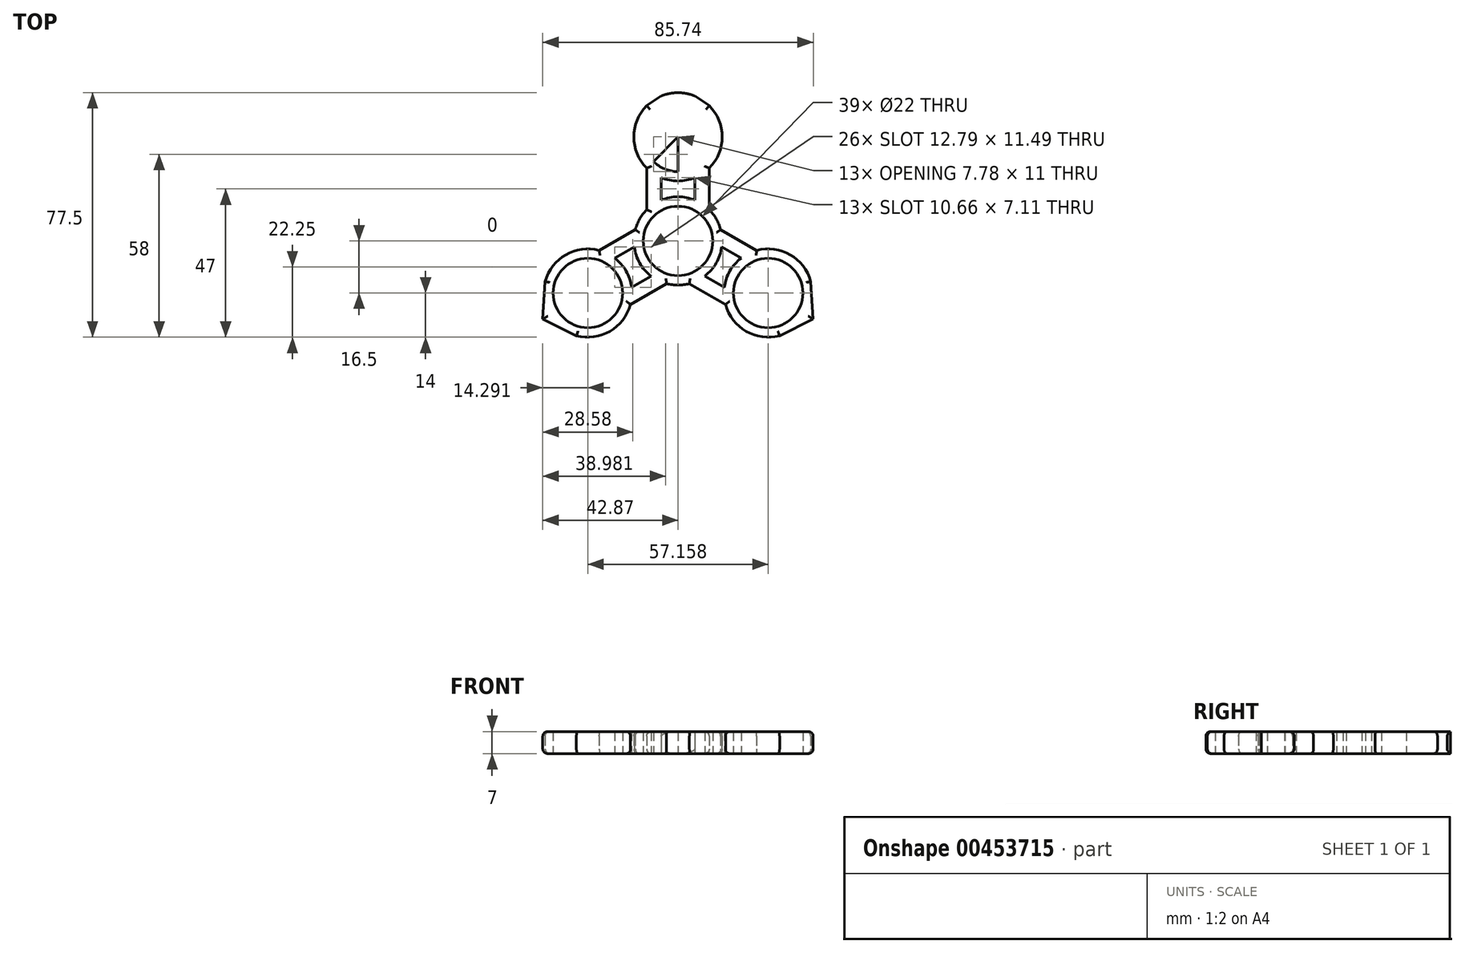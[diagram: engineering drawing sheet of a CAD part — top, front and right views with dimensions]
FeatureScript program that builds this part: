
annotation { "Feature Type Name" : "Feature", "Feature Type Description" : "" }
export const myFeature = defineFeature(function(context is Context, id is Id, definition is map)
    precondition{}
    {
        {
            var Q0;
            Q0=qCreatedBy(makeId("Top.planeOp"),FACE);
            var sketch = newSketch(context, id + "F0", { "sketchPlane" : qUnion([Q0])});
            skCircle(sketch, "E0", {"center": v(0, 0) * mm, "radius": 11 * mm});
            skArc(sketch, "E1.0", {"start": v(-9.9, 9.9) * mm, "mid": v(0, -14) * mm, "end": v(9.9, 9.9) * mm});
            skLineSegment(sketch, "E2", {"start": v(0, 0) * mm, "end": v(9.9, 9.9) * mm});
            skLineSegment(sketch, "E3.MirrorCS", {"start": v(0, 0) * mm, "end": v(-9.9, 9.9) * mm});
            skLineSegment(sketch, "E4", {"start": v(0, 0) * mm, "end": v(0, 16.5) * mm});
            skLineSegment(sketch, "E5", {"start": v(-9.9, 9.9) * mm, "end": v(0, 16.5) * mm});
            skLineSegment(sketch, "E6", {"start": v(0, 16.5) * mm, "end": v(9.9, 9.9) * mm});
            skLineSegment(sketch, "E7", {"start": v(0, 16.5) * mm, "end": v(16.35, 16.5) * mm});
            skLineSegment(sketch, "E8.MirrorCS", {"start": v(0, 33) * mm, "end": v(9.9, 23.1) * mm});
            skCircle(sketch, "E9.MirrorC", {"center": v(0, 33) * mm, "radius": 11 * mm});
            skArc(sketch, "E10.MirrorC", {"start": v(5.33, 20.06) * mm, "mid": v(0, 19) * mm, "end": v(-5.33, 20.06) * mm});
            skLineSegment(sketch, "E11.MirrorCS", {"start": v(0, 33) * mm, "end": v(0, 16.5) * mm});
            skLineSegment(sketch, "E12.MirrorCS", {"start": v(0, 33) * mm, "end": v(-9.9, 23.1) * mm});
            skLineSegment(sketch, "E13.MirrorCS", {"start": v(-9.9, 23.1) * mm, "end": v(0, 16.5) * mm});
            skLineSegment(sketch, "E14.MirrorCS", {"start": v(0, 16.5) * mm, "end": v(9.9, 23.1) * mm});
            skArc(sketch, "E15.trimOffspring", {"start": v(5.33, 12.94) * mm, "mid": v(0, 14) * mm, "end": v(-5.33, 12.94) * mm});
            skArc(sketch, "E16.trimOffspring", {"start": v(-9.9, 23.1) * mm, "mid": v(-14, 33) * mm, "end": v(-9.9, 42.9) * mm});
            skLineSegment(sketch, "E17", {"start": v(5.33, 20.06) * mm, "end": v(5.33, 12.94) * mm});
            skLineSegment(sketch, "E18", {"start": v(9.9, 23.1) * mm, "end": v(9.9, 9.9) * mm});
            skLineSegment(sketch, "E19", {"start": v(-9.9, 23.1) * mm, "end": v(-9.9, 9.9) * mm});
            skLineSegment(sketch, "E20", {"start": v(-5.33, 12.94) * mm, "end": v(-5.33, 20.06) * mm});
            skLineSegment(sketch, "E21", {"start": v(0, 33) * mm, "end": v(7.48, 33) * mm});
            skLineSegment(sketch, "E22.MirrorCS", {"start": v(0, 49.5) * mm, "end": v(9.9, 42.9) * mm});
            skLineSegment(sketch, "E23.MirrorCS", {"start": v(-9.9, 42.9) * mm, "end": v(0, 49.5) * mm});
            skArc(sketch, "E24.trimOffspring", {"start": v(-5.33, 45.94) * mm, "mid": v(0, 47) * mm, "end": v(5.33, 45.94) * mm});
            skArc(sketch, "E25.trimOffspring", {"start": v(9.9, 42.9) * mm, "mid": v(14, 33) * mm, "end": v(9.9, 23.1) * mm});
            skLineSegment(sketch, "E26.1.0", {"start": v(-32.2, -30.02) * mm, "end": v(-42.87, -24.75) * mm});
            skLineSegment(sketch, "E26.1.1", {"start": v(-42.87, -24.75) * mm, "end": v(-42.1, -12.88) * mm});
            skArc(sketch, "E26.1.2", {"start": v(-37.12, -27.6) * mm, "mid": v(-40.7, -23.5) * mm, "end": v(-42.46, -18.35) * mm});
            skArc(sketch, "E26.1.3", {"start": v(-42.1, -12.88) * mm, "mid": v(-35.58, -4.38) * mm, "end": v(-24.96, -2.98) * mm});
            skCircle(sketch, "E26.1.4", {"center": v(-28.58, -16.5) * mm, "radius": 11 * mm});
            skArc(sketch, "E26.1.5", {"start": v(-15.06, -20.12) * mm, "mid": v(-21.58, -28.62) * mm, "end": v(-32.2, -30.02) * mm});
            skLineSegment(sketch, "E26.1.6", {"start": v(-15.06, -20.12) * mm, "end": v(-14.29, -8.25) * mm});
            skArc(sketch, "E26.1.7", {"start": v(-20.03, -5.4) * mm, "mid": v(-16.45, -9.5) * mm, "end": v(-14.7, -14.65) * mm});
            skLineSegment(sketch, "E26.1.8", {"start": v(-20.03, -5.4) * mm, "end": v(-13.88, -1.85) * mm});
            skLineSegment(sketch, "E26.1.9", {"start": v(-24.96, -2.98) * mm, "end": v(-13.52, 3.62) * mm});
            skLineSegment(sketch, "E26.1.10", {"start": v(-14.29, -8.25) * mm, "end": v(-24.96, -2.98) * mm});
            skLineSegment(sketch, "E26.2.0", {"start": v(42.1, -12.88) * mm, "end": v(42.87, -24.75) * mm});
            skLineSegment(sketch, "E26.2.1", {"start": v(42.87, -24.75) * mm, "end": v(32.2, -30.02) * mm});
            skArc(sketch, "E26.2.2", {"start": v(42.46, -18.35) * mm, "mid": v(40.7, -23.5) * mm, "end": v(37.12, -27.6) * mm});
            skArc(sketch, "E26.2.3", {"start": v(32.2, -30.02) * mm, "mid": v(21.58, -28.62) * mm, "end": v(15.06, -20.12) * mm});
            skCircle(sketch, "E26.2.4", {"center": v(28.58, -16.5) * mm, "radius": 11 * mm});
            skArc(sketch, "E26.2.5", {"start": v(24.96, -2.98) * mm, "mid": v(35.58, -4.38) * mm, "end": v(42.1, -12.88) * mm});
            skLineSegment(sketch, "E26.2.6", {"start": v(24.96, -2.98) * mm, "end": v(14.29, -8.25) * mm});
            skArc(sketch, "E26.2.7", {"start": v(14.7, -14.65) * mm, "mid": v(16.45, -9.5) * mm, "end": v(20.03, -5.4) * mm});
            skLineSegment(sketch, "E26.2.8", {"start": v(14.7, -14.65) * mm, "end": v(8.54, -11.1) * mm});
            skLineSegment(sketch, "E26.2.9", {"start": v(15.06, -20.12) * mm, "end": v(3.62, -13.52) * mm});
            skLineSegment(sketch, "E26.2.10", {"start": v(14.29, -8.25) * mm, "end": v(15.06, -20.12) * mm});
            skLineSegment(sketch, "E27.1.0", {"start": v(-8.54, -11.1) * mm, "end": v(-14.7, -14.65) * mm});
            skLineSegment(sketch, "E27.1.1", {"start": v(-15.06, -20.12) * mm, "end": v(-3.62, -13.52) * mm});
            skLineSegment(sketch, "E27.2.0", {"start": v(13.88, -1.85) * mm, "end": v(20.03, -5.4) * mm});
            skLineSegment(sketch, "E27.2.1", {"start": v(24.96, -2.98) * mm, "end": v(13.52, 3.62) * mm});
            skSolve(sketch);
        }
        {
            var Q0;
            {var subQ3=sQuery(id+"F0.wireOp",EDGE,"E24.trimOffspring");Q0=makeQuery(id+"F0.imprint","IMPRINT",FACE,{"disambiguationData":[TD([[makeQuery(id+"F0.imprint","IMPRINT",EDGE,{"derivedFrom":subQ3}),1.0]])]});}
            var Q1;
            {var subQ0=sQuery(id+"F0.wireOp",EDGE,"E16.trimOffspring");Q1=makeQuery(id+"F0.imprint","IMPRINT",FACE,{"disambiguationData":[TD([[makeQuery(id+"F0.imprint","IMPRINT",EDGE,{"derivedFrom":subQ0}),-1.0]])]});}
            var Q2;
            {var subQ1=sQuery(id+"F0.wireOp",EDGE,"E9.MirrorC");var subQ7=sQuery(id+"F0.wireOp",EDGE,"E8.MirrorCS");var subQ8=makeQuery(id+"F0.imprint","INTERSECT",VERTEX,{"derivedFrom":[subQ7,subQ1]});Q2=makeQuery(id+"F0.imprint","IMPRINT",FACE,{"disambiguationData":[TD([[makeQuery(id+"F0.imprint","IMPRINT",EDGE,{"disambiguationData":[TD([[subQ8,-1.0]])],"derivedFrom":subQ1}),1.0]])]});}
            var Q3;
            {var subQ3=sQuery(id+"F0.wireOp",EDGE,"E9.MirrorC");var subQ7=sQuery(id+"F0.wireOp",EDGE,"E11.MirrorCS");var subQ9=makeQuery(id+"F0.imprint","INTERSECT",VERTEX,{"derivedFrom":[subQ3,subQ7]});Q3=makeQuery(id+"F0.imprint","IMPRINT",FACE,{"disambiguationData":[TD([[makeQuery(id+"F0.imprint","IMPRINT",EDGE,{"disambiguationData":[TD([[subQ9,-1.0]])],"derivedFrom":subQ3}),1.0]])]});}
            var Q4;
            {var subQ0=sQuery(id+"F0.wireOp",EDGE,"E19");Q4=makeQuery(id+"F0.imprint","IMPRINT",FACE,{"disambiguationData":[TD([[makeQuery(id+"F0.imprint","IMPRINT",EDGE,{"derivedFrom":subQ0}),1.0]])]});}
            var Q5;
            {var subQ0=sQuery(id+"F0.wireOp",EDGE,"E18");var subQ5=sQuery(id+"F0.wireOp",EDGE,"E7");var subQ6=makeQuery(id+"F0.imprint","INTERSECT",VERTEX,{"derivedFrom":[subQ5,subQ0]});Q5=makeQuery(id+"F0.imprint","IMPRINT",FACE,{"disambiguationData":[TD([[makeQuery(id+"F0.imprint","IMPRINT",EDGE,{"disambiguationData":[TD([[subQ6,1.0]])],"derivedFrom":subQ5}),-1.0]])]});}
            var Q6;
            {var subQ0=sQuery(id+"F0.wireOp",EDGE,"E18");var subQ1=sQuery(id+"F0.wireOp",EDGE,"E7");var subQ2=makeQuery(id+"F0.imprint","INTERSECT",VERTEX,{"derivedFrom":[subQ1,subQ0]});Q6=makeQuery(id+"F0.imprint","IMPRINT",FACE,{"disambiguationData":[TD([[makeQuery(id+"F0.imprint","IMPRINT",EDGE,{"disambiguationData":[TD([[subQ2,1.0]])],"derivedFrom":subQ1}),1.0]])]});}
            var Q7;
            {var subQ5=sQuery(id+"F0.wireOp",EDGE,"E4");var subQ6=sQuery(id+"F0.wireOp",EDGE,"E0");var subQ7=makeQuery(id+"F0.imprint","INTERSECT",VERTEX,{"derivedFrom":[subQ6,subQ5]});Q7=makeQuery(id+"F0.imprint","IMPRINT",FACE,{"disambiguationData":[TD([[makeQuery(id+"F0.imprint","IMPRINT",EDGE,{"disambiguationData":[TD([[subQ7,1.0]])],"derivedFrom":subQ6}),-1.0]])]});}
            var Q8;
            {var subQ5=sQuery(id+"F0.wireOp",EDGE,"E4");var subQ6=sQuery(id+"F0.wireOp",EDGE,"E0");var subQ7=makeQuery(id+"F0.imprint","INTERSECT",VERTEX,{"derivedFrom":[subQ6,subQ5]});Q8=makeQuery(id+"F0.imprint","IMPRINT",FACE,{"disambiguationData":[TD([[makeQuery(id+"F0.imprint","IMPRINT",EDGE,{"disambiguationData":[TD([[subQ7,-1.0]])],"derivedFrom":subQ6}),-1.0]])]});}
            var Q9;
            {var subQ0=sQuery(id+"F0.wireOp",EDGE,"E2");var subQ9=sQuery(id+"F0.wireOp",EDGE,"E0");var subQ10=makeQuery(id+"F0.imprint","INTERSECT",VERTEX,{"derivedFrom":[subQ9,subQ0]});Q9=makeQuery(id+"F0.imprint","IMPRINT",FACE,{"disambiguationData":[TD([[makeQuery(id+"F0.imprint","IMPRINT",EDGE,{"disambiguationData":[TD([[subQ10,1.0]])],"derivedFrom":subQ9}),-1.0]])]});}
            var Q10;
            {var subQ0=sQuery(id+"F0.wireOp",EDGE,"E26.1.8");Q10=makeQuery(id+"F0.imprint","IMPRINT",FACE,{"disambiguationData":[TD([[makeQuery(id+"F0.imprint","IMPRINT",EDGE,{"derivedFrom":subQ0}),1.0]])]});}
            var Q11;
            {var subQ0=sQuery(id+"F0.wireOp",EDGE,"E27.1.0");Q11=makeQuery(id+"F0.imprint","IMPRINT",FACE,{"disambiguationData":[TD([[makeQuery(id+"F0.imprint","IMPRINT",EDGE,{"derivedFrom":subQ0}),1.0]])]});}
            var Q12;
            {var subQ3=sQuery(id+"F0.wireOp",EDGE,"E26.1.7");Q12=makeQuery(id+"F0.imprint","IMPRINT",FACE,{"disambiguationData":[TD([[makeQuery(id+"F0.imprint","IMPRINT",EDGE,{"derivedFrom":subQ3}),1.0]])]});}
            var Q13;
            {var subQ0=sQuery(id+"F0.wireOp",EDGE,"E26.1.2");Q13=makeQuery(id+"F0.imprint","IMPRINT",FACE,{"disambiguationData":[TD([[makeQuery(id+"F0.imprint","IMPRINT",EDGE,{"derivedFrom":subQ0}),-1.0]])]});}
            var Q14;
            {var subQ3=sQuery(id+"F0.wireOp",EDGE,"E26.1.2");Q14=makeQuery(id+"F0.imprint","IMPRINT",FACE,{"disambiguationData":[TD([[makeQuery(id+"F0.imprint","IMPRINT",EDGE,{"derivedFrom":subQ3}),1.0]])]});}
            var Q15;
            {var subQ0=sQuery(id+"F0.wireOp",EDGE,"E26.2.8");Q15=makeQuery(id+"F0.imprint","IMPRINT",FACE,{"disambiguationData":[TD([[makeQuery(id+"F0.imprint","IMPRINT",EDGE,{"derivedFrom":subQ0}),1.0]])]});}
            var Q16;
            {var subQ0=sQuery(id+"F0.wireOp",EDGE,"E27.2.0");Q16=makeQuery(id+"F0.imprint","IMPRINT",FACE,{"disambiguationData":[TD([[makeQuery(id+"F0.imprint","IMPRINT",EDGE,{"derivedFrom":subQ0}),1.0]])]});}
            var Q17;
            {var subQ3=sQuery(id+"F0.wireOp",EDGE,"E26.2.7");Q17=makeQuery(id+"F0.imprint","IMPRINT",FACE,{"disambiguationData":[TD([[makeQuery(id+"F0.imprint","IMPRINT",EDGE,{"derivedFrom":subQ3}),1.0]])]});}
            var Q18;
            {var subQ0=sQuery(id+"F0.wireOp",EDGE,"E26.2.2");Q18=makeQuery(id+"F0.imprint","IMPRINT",FACE,{"disambiguationData":[TD([[makeQuery(id+"F0.imprint","IMPRINT",EDGE,{"derivedFrom":subQ0}),-1.0]])]});}
            var Q19;
            {var subQ3=sQuery(id+"F0.wireOp",EDGE,"E26.2.2");Q19=makeQuery(id+"F0.imprint","IMPRINT",FACE,{"disambiguationData":[TD([[makeQuery(id+"F0.imprint","IMPRINT",EDGE,{"derivedFrom":subQ3}),1.0]])]});}
            var Q20;
            {var subQ1=sQuery(id+"F0.wireOp",EDGE,"E10.MirrorC");var subQ3=sQuery(id+"F0.wireOp",EDGE,"E11.MirrorCS");var subQ4=makeQuery(id+"F0.imprint","INTERSECT",VERTEX,{"derivedFrom":[subQ1,subQ3]});Q20=makeQuery(id+"F0.imprint","IMPRINT",FACE,{"disambiguationData":[TD([[makeQuery(id+"F0.imprint","IMPRINT",EDGE,{"disambiguationData":[TD([[subQ4,-1.0]])],"derivedFrom":subQ1}),1.0]])]});}
            var Q21;
            {var subQ1=sQuery(id+"F0.wireOp",EDGE,"E10.MirrorC");var subQ3=sQuery(id+"F0.wireOp",EDGE,"E11.MirrorCS");var subQ4=makeQuery(id+"F0.imprint","INTERSECT",VERTEX,{"derivedFrom":[subQ1,subQ3]});Q21=makeQuery(id+"F0.imprint","IMPRINT",FACE,{"disambiguationData":[TD([[makeQuery(id+"F0.imprint","IMPRINT",EDGE,{"disambiguationData":[TD([[subQ4,1.0]])],"derivedFrom":subQ1}),1.0]])]});}
            extrude(context, id + "F1", {"entities" : qUnion([Q0, Q1, Q2, Q3, Q4, Q5, Q6, Q7, Q8, Q9, Q10, Q11, Q12, Q13, Q14, Q15, Q16, Q17, Q18, Q19, Q20, Q21]), "depth" : 7 * mm});
        }
        {
            var Q0;
            Q0=makeQuery(id+"F1.opExtrude","CAP_EDGE",EDGE,{"disambiguationData":[OSD([sQuery(id+"F0.wireOp",EDGE,"E16.trimOffspring")])],"isStart":false});
            var Q1;
            Q1=makeQuery(id+"F1.opExtrude","CAP_EDGE",EDGE,{"disambiguationData":[OSD([sQuery(id+"F0.wireOp",EDGE,"E23.MirrorCS")])],"isStart":false});
            var Q2;
            Q2=makeQuery(id+"F1.opExtrude","CAP_EDGE",EDGE,{"disambiguationData":[OSD([sQuery(id+"F0.wireOp",EDGE,"E22.MirrorCS")])],"isStart":false});
            var Q3;
            Q3=makeQuery(id+"F1.opExtrude","CAP_EDGE",EDGE,{"disambiguationData":[OSD([sQuery(id+"F0.wireOp",EDGE,"E25.trimOffspring")])],"isStart":false});
            var Q4;
            Q4=makeQuery(id+"F1.opExtrude","CAP_EDGE",EDGE,{"disambiguationData":[OSD([sQuery(id+"F0.wireOp",EDGE,"E18")])],"isStart":false});
            var Q5;
            {var subQ0=sQuery(id+"F0.wireOp",EDGE,"E1.0");Q5=makeQuery(id+"F1.opExtrude","CAP_EDGE",EDGE,{"disambiguationData":[OSD([subQ0]),TDD([makeQuery(id+"F0.imprint","IMPRINT",EDGE,{"disambiguationData":[TD([[makeQuery(id+"F0.imprint","INTERSECT",VERTEX,{"derivedFrom":[subQ0,sQuery(id+"F0.wireOp",EDGE,"E27.2.1")]}),-1.0]])],"derivedFrom":subQ0})])],"isStart":false});}
            var Q6;
            Q6=makeQuery(id+"F1.opExtrude","CAP_EDGE",EDGE,{"disambiguationData":[OSD([sQuery(id+"F0.wireOp",EDGE,"E27.2.1")])],"isStart":false});
            var Q7;
            Q7=makeQuery(id+"F1.opExtrude","CAP_EDGE",EDGE,{"disambiguationData":[OSD([sQuery(id+"F0.wireOp",EDGE,"E26.2.5")])],"isStart":false});
            var Q8;
            Q8=makeQuery(id+"F1.opExtrude","CAP_EDGE",EDGE,{"disambiguationData":[OSD([sQuery(id+"F0.wireOp",EDGE,"E26.2.0")])],"isStart":false});
            var Q9;
            Q9=makeQuery(id+"F1.opExtrude","CAP_EDGE",EDGE,{"disambiguationData":[OSD([sQuery(id+"F0.wireOp",EDGE,"E26.2.1")])],"isStart":false});
            var Q10;
            Q10=makeQuery(id+"F1.opExtrude","CAP_EDGE",EDGE,{"disambiguationData":[OSD([sQuery(id+"F0.wireOp",EDGE,"E26.2.3")])],"isStart":false});
            var Q11;
            Q11=makeQuery(id+"F1.opExtrude","CAP_EDGE",EDGE,{"disambiguationData":[OSD([sQuery(id+"F0.wireOp",EDGE,"E26.2.9")])],"isStart":false});
            var Q12;
            {var subQ0=sQuery(id+"F0.wireOp",EDGE,"E1.0");Q12=makeQuery(id+"F1.opExtrude","CAP_EDGE",EDGE,{"disambiguationData":[OSD([subQ0]),TDD([makeQuery(id+"F0.imprint","IMPRINT",EDGE,{"disambiguationData":[TD([[makeQuery(id+"F0.imprint","INTERSECT",VERTEX,{"derivedFrom":[subQ0,sQuery(id+"F0.wireOp",EDGE,"E26.2.9")]}),1.0]])],"derivedFrom":subQ0})])],"isStart":false});}
            var Q13;
            Q13=makeQuery(id+"F1.opExtrude","CAP_EDGE",EDGE,{"disambiguationData":[OSD([sQuery(id+"F0.wireOp",EDGE,"E27.1.1")])],"isStart":false});
            var Q14;
            Q14=makeQuery(id+"F1.opExtrude","CAP_EDGE",EDGE,{"disambiguationData":[OSD([sQuery(id+"F0.wireOp",EDGE,"E26.1.5")])],"isStart":false});
            var Q15;
            Q15=makeQuery(id+"F1.opExtrude","CAP_EDGE",EDGE,{"disambiguationData":[OSD([sQuery(id+"F0.wireOp",EDGE,"E26.1.0")])],"isStart":false});
            var Q16;
            Q16=makeQuery(id+"F1.opExtrude","CAP_EDGE",EDGE,{"disambiguationData":[OSD([sQuery(id+"F0.wireOp",EDGE,"E26.1.1")])],"isStart":false});
            var Q17;
            Q17=makeQuery(id+"F1.opExtrude","CAP_EDGE",EDGE,{"disambiguationData":[OSD([sQuery(id+"F0.wireOp",EDGE,"E26.1.3")])],"isStart":false});
            var Q18;
            Q18=makeQuery(id+"F1.opExtrude","CAP_EDGE",EDGE,{"disambiguationData":[OSD([sQuery(id+"F0.wireOp",EDGE,"E26.1.9")])],"isStart":false});
            var Q19;
            Q19=makeQuery(id+"F1.opExtrude","CAP_EDGE",EDGE,{"disambiguationData":[OSD([sQuery(id+"F0.wireOp",EDGE,"E19")])],"isStart":false});
            var Q20;
            {var subQ0=sQuery(id+"F0.wireOp",EDGE,"E1.0");Q20=makeQuery(id+"F1.opExtrude","CAP_EDGE",EDGE,{"disambiguationData":[OSD([subQ0]),TDD([makeQuery(id+"F0.imprint","IMPRINT",EDGE,{"disambiguationData":[TD([[makeQuery(id+"F0.imprint","INTERSECT",VERTEX,{"derivedFrom":[subQ0,sQuery(id+"F0.wireOp",EDGE,"E26.1.9")]}),1.0]])],"derivedFrom":subQ0})])],"isStart":false});}
            var Q21;
            Q21=makeQuery(id+"F1.opExtrude","CAP_EDGE",EDGE,{"disambiguationData":[OSD([sQuery(id+"F0.wireOp",EDGE,"E26.2.9")])],"isStart":true});
            var Q22;
            Q22=makeQuery(id+"F1.opExtrude","CAP_EDGE",EDGE,{"disambiguationData":[OSD([sQuery(id+"F0.wireOp",EDGE,"E26.2.3")])],"isStart":true});
            var Q23;
            Q23=makeQuery(id+"F1.opExtrude","CAP_EDGE",EDGE,{"disambiguationData":[OSD([sQuery(id+"F0.wireOp",EDGE,"E26.2.1")])],"isStart":true});
            var Q24;
            Q24=makeQuery(id+"F1.opExtrude","CAP_EDGE",EDGE,{"disambiguationData":[OSD([sQuery(id+"F0.wireOp",EDGE,"E26.2.0")])],"isStart":true});
            var Q25;
            Q25=makeQuery(id+"F1.opExtrude","CAP_EDGE",EDGE,{"disambiguationData":[OSD([sQuery(id+"F0.wireOp",EDGE,"E26.2.5")])],"isStart":true});
            var Q26;
            Q26=makeQuery(id+"F1.opExtrude","CAP_EDGE",EDGE,{"disambiguationData":[OSD([sQuery(id+"F0.wireOp",EDGE,"E27.2.1")])],"isStart":true});
            var Q27;
            {var subQ0=sQuery(id+"F0.wireOp",EDGE,"E1.0");Q27=makeQuery(id+"F1.opExtrude","CAP_EDGE",EDGE,{"disambiguationData":[OSD([subQ0]),TDD([makeQuery(id+"F0.imprint","IMPRINT",EDGE,{"disambiguationData":[TD([[makeQuery(id+"F0.imprint","INTERSECT",VERTEX,{"derivedFrom":[subQ0,sQuery(id+"F0.wireOp",EDGE,"E27.2.1")]}),-1.0]])],"derivedFrom":subQ0})])],"isStart":true});}
            var Q28;
            Q28=makeQuery(id+"F1.opExtrude","CAP_EDGE",EDGE,{"disambiguationData":[OSD([sQuery(id+"F0.wireOp",EDGE,"E18")])],"isStart":true});
            var Q29;
            Q29=makeQuery(id+"F1.opExtrude","CAP_EDGE",EDGE,{"disambiguationData":[OSD([sQuery(id+"F0.wireOp",EDGE,"E25.trimOffspring")])],"isStart":true});
            var Q30;
            Q30=makeQuery(id+"F1.opExtrude","CAP_EDGE",EDGE,{"disambiguationData":[OSD([sQuery(id+"F0.wireOp",EDGE,"E22.MirrorCS")])],"isStart":true});
            var Q31;
            Q31=makeQuery(id+"F1.opExtrude","CAP_EDGE",EDGE,{"disambiguationData":[OSD([sQuery(id+"F0.wireOp",EDGE,"E23.MirrorCS")])],"isStart":true});
            var Q32;
            Q32=makeQuery(id+"F1.opExtrude","CAP_EDGE",EDGE,{"disambiguationData":[OSD([sQuery(id+"F0.wireOp",EDGE,"E16.trimOffspring")])],"isStart":true});
            var Q33;
            Q33=makeQuery(id+"F1.opExtrude","CAP_EDGE",EDGE,{"disambiguationData":[OSD([sQuery(id+"F0.wireOp",EDGE,"E19")])],"isStart":true});
            var Q34;
            {var subQ0=sQuery(id+"F0.wireOp",EDGE,"E1.0");Q34=makeQuery(id+"F1.opExtrude","CAP_EDGE",EDGE,{"disambiguationData":[OSD([subQ0]),TDD([makeQuery(id+"F0.imprint","IMPRINT",EDGE,{"disambiguationData":[TD([[makeQuery(id+"F0.imprint","INTERSECT",VERTEX,{"derivedFrom":[subQ0,sQuery(id+"F0.wireOp",EDGE,"E26.1.9")]}),1.0]])],"derivedFrom":subQ0})])],"isStart":true});}
            var Q35;
            Q35=makeQuery(id+"F1.opExtrude","CAP_EDGE",EDGE,{"disambiguationData":[OSD([sQuery(id+"F0.wireOp",EDGE,"E26.1.9")])],"isStart":true});
            var Q36;
            Q36=makeQuery(id+"F1.opExtrude","CAP_EDGE",EDGE,{"disambiguationData":[OSD([sQuery(id+"F0.wireOp",EDGE,"E26.1.3")])],"isStart":true});
            var Q37;
            Q37=makeQuery(id+"F1.opExtrude","CAP_EDGE",EDGE,{"disambiguationData":[OSD([sQuery(id+"F0.wireOp",EDGE,"E26.1.1")])],"isStart":true});
            var Q38;
            Q38=makeQuery(id+"F1.opExtrude","CAP_EDGE",EDGE,{"disambiguationData":[OSD([sQuery(id+"F0.wireOp",EDGE,"E26.1.0")])],"isStart":true});
            var Q39;
            Q39=makeQuery(id+"F1.opExtrude","CAP_EDGE",EDGE,{"disambiguationData":[OSD([sQuery(id+"F0.wireOp",EDGE,"E26.1.5")])],"isStart":true});
            var Q40;
            {var subQ0=sQuery(id+"F0.wireOp",EDGE,"E1.0");Q40=makeQuery(id+"F1.opExtrude","CAP_EDGE",EDGE,{"disambiguationData":[OSD([subQ0]),TDD([makeQuery(id+"F0.imprint","IMPRINT",EDGE,{"disambiguationData":[TD([[makeQuery(id+"F0.imprint","INTERSECT",VERTEX,{"derivedFrom":[subQ0,sQuery(id+"F0.wireOp",EDGE,"E26.2.9")]}),1.0]])],"derivedFrom":subQ0})])],"isStart":true});}
            var Q41;
            Q41=makeQuery(id+"F1.opExtrude","CAP_EDGE",EDGE,{"disambiguationData":[OSD([sQuery(id+"F0.wireOp",EDGE,"E27.1.1")])],"isStart":true});
            fillet(context, id + "F2", {"entities" : qUnion([Q0, Q1, Q2, Q3, Q4, Q5, Q6, Q7, Q8, Q9, Q10, Q11, Q12, Q13, Q14, Q15, Q16, Q17, Q18, Q19, Q20, Q21, Q22, Q23, Q24, Q25, Q26, Q27, Q28, Q29, Q30, Q31, Q32, Q33, Q34, Q35, Q36, Q37, Q38, Q39, Q40, Q41]), "radius" : 1.5 * mm, "tangentPropagation" : true, "allowEdgeOverflow" : false});
        }
    });
